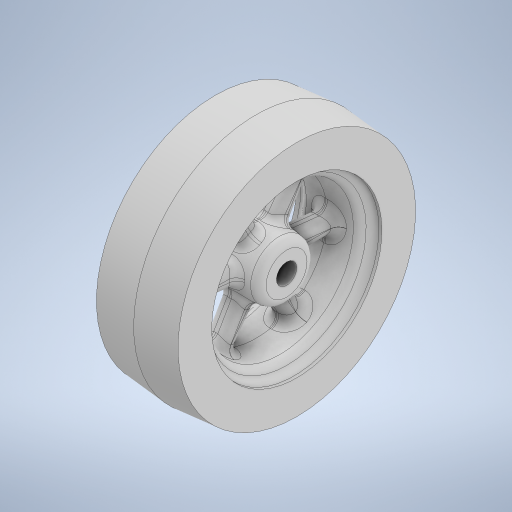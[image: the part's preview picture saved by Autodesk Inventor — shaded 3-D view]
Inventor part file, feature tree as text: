
AUTODESK INVENTOR PART (.ipt)
format: ipt  version: 2023 (Build 270158000, 158)  size: 1,291,264 bytes
history: native  units: in
note: dims shown in document units (in); Inventor stores cm internally (conversion verified against a paired STEP export)
features: extrude x3, sketch x2, fillet x2, draft x1
ambient origin geometry x8: Origin, YZ Plane, XZ Plane, XY Plane, X Axis, Y Axis, Z Axis, Center Point
bodies: Body1 (feature_tree)
feature tree (8):
  sketch  "Sketch1"  dims[d29=0.125in d31=2.0in d32=3.0in]
  extrude  "Extrusion7"  Depth=3.0in
  extrude  "Extrusion8"  Depth=0.1in
  extrude  "Extrusion9"  Depth=0.1in
  sketch  "Sketch3"  dims[d33=0.75in d34=0.25in d35=1.75in d37=2.3622in d39=360.0deg d41=1.0in d42=0.0in d43=0.75in d44=0.0in d45=0.25in d46=0.0in d54=0.0344in d55=0.1in d56=0.1in]
  draft  "FaceDraft2"
  fillet  "Fillet5"  Radius=2.3622in
  fillet  "Fillet6"  Radius=1.0in
